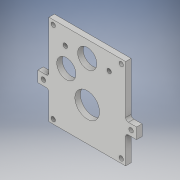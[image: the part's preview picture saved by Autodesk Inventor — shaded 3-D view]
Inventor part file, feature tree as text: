
AUTODESK INVENTOR PART (.ipt)
format: ipt  version: 2018 (Build 220112000, 112)  size: 177,664 bytes
history: native  units: in
note: dims shown in document units (in); Inventor stores cm internally (conversion verified against a paired STEP export)
features: extrude x3, sketch x3, fillet x1
ambient origin geometry x8: Origin, YZ Plane, XZ Plane, XY Plane, X Axis, Y Axis, Z Axis, Center Point
bodies: Solid1 (feature_tree)
feature tree (7):
  extrude  "Extrusion1"  Depth=1.35in
  extrude  "Extrusion2"  Depth=0.875in
  extrude  "Extrusion3"  Depth=0.125in
  fillet  "Fillet1"  Radius=1.0in
  sketch  "Sketch1"  dims[d0=1.125in d1=1.35in]
  sketch  "Sketch2"  dims[d2=135.0deg d3=0.875in]
  sketch  "Sketch3"  dims[d7=0.882in d8=0.875in d9=1.0in d10=2.0in d11=0.2031in d12=0.75in d13=4.125in d14=1.75in d15=0.25in d16=0.0in d17=1.75in d18=0.2in d19=0.2in d20=0.2031in d21=1.0in d22=0.0in d23=0.2031in d24=0.25in d25=0.5in d26=0.5in d27=0.2031in d28=0.25in d29=0.0in d30=0.125in]
